FCSTD DOCUMENT  (FreeCAD 0.14R3700 (Git))
Label: TMP_outils_FV-082
License: CC-BY 3.0
LicenseURL: http://creativecommons.org/licenses/by/3.0/
objects: Sketcher::SketchObject×1
note: 1 computed .brp shape members not serialized (recipe doc carries the construction recipe); baked Part::Feature solids carry a one-line shape summary decoded from their .brp

FEATURE [Sketcher::SketchObject] Sketch
  Placement = pos=(0,0,0) rot=(-1,0,0;4.71239rad)
  sketch-geometry (10):
    g0: LineSegment StartX=-30 StartY=115 StartZ=0 EndX=-85 EndY=115 EndZ=0
    g1: LineSegment StartX=-85 StartY=115 StartZ=0 EndX=-85 EndY=65 EndZ=0
    g2: LineSegment StartX=-85 StartY=65 StartZ=0 EndX=0 EndY=65 EndZ=0
    g3: LineSegment StartX=0 StartY=65 StartZ=0 EndX=0 EndY=0 EndZ=0
    g4: LineSegment StartX=0 StartY=0 StartZ=0 EndX=25 EndY=0 EndZ=0
    g5: LineSegment StartX=25 StartY=0 StartZ=0 EndX=25 EndY=75 EndZ=0
    g6: LineSegment StartX=25 StartY=75 StartZ=0 EndX=-75 EndY=75 EndZ=0
    g7: LineSegment StartX=-75 StartY=75 StartZ=0 EndX=-75 EndY=105 EndZ=0
    g8: LineSegment StartX=-75 StartY=105 StartZ=0 EndX=-30 EndY=105 EndZ=0
    g9: LineSegment StartX=-30 StartY=105 StartZ=0 EndX=-30 EndY=115 EndZ=0
  constraints (30):
    c: Horizontal(g0)
    c: Coincident(g1,g0)
    c: Vertical(g1)
    c: Coincident(g2,g1)
    c: Horizontal(g2)
    c: Coincident(g3,g2)
    c: Vertical(g3)
    c: Coincident(g4,g3)
    c: Horizontal(g4)
    c: Vertical(g5)
    c: Coincident(g6,g5)
    c: Horizontal(g6)
    c: Coincident(g7,g6)
    c: Vertical(g7)
    c: Coincident(g8,g7)
    c: Horizontal(g8)
    c: Coincident(g9,g8)
    c: Coincident(g9,g0)
    c: Distance(g0) = 55
    c: Distance(g4) = 25
    c: Distance(g5) = 75
    c: Distance(g3) = 65
    c: Distance(g1) = 50
    c: Distance(g9) = 10
    c: Coincident(g5,g4)
    c: Coincident(g3,g-1)
    c: Distance(g2) = 85
    c: Distance(g8) = 45
    c: Angle(g9,g8) = 1.5708
    c: Angle(g0,g9) = 1.5708
